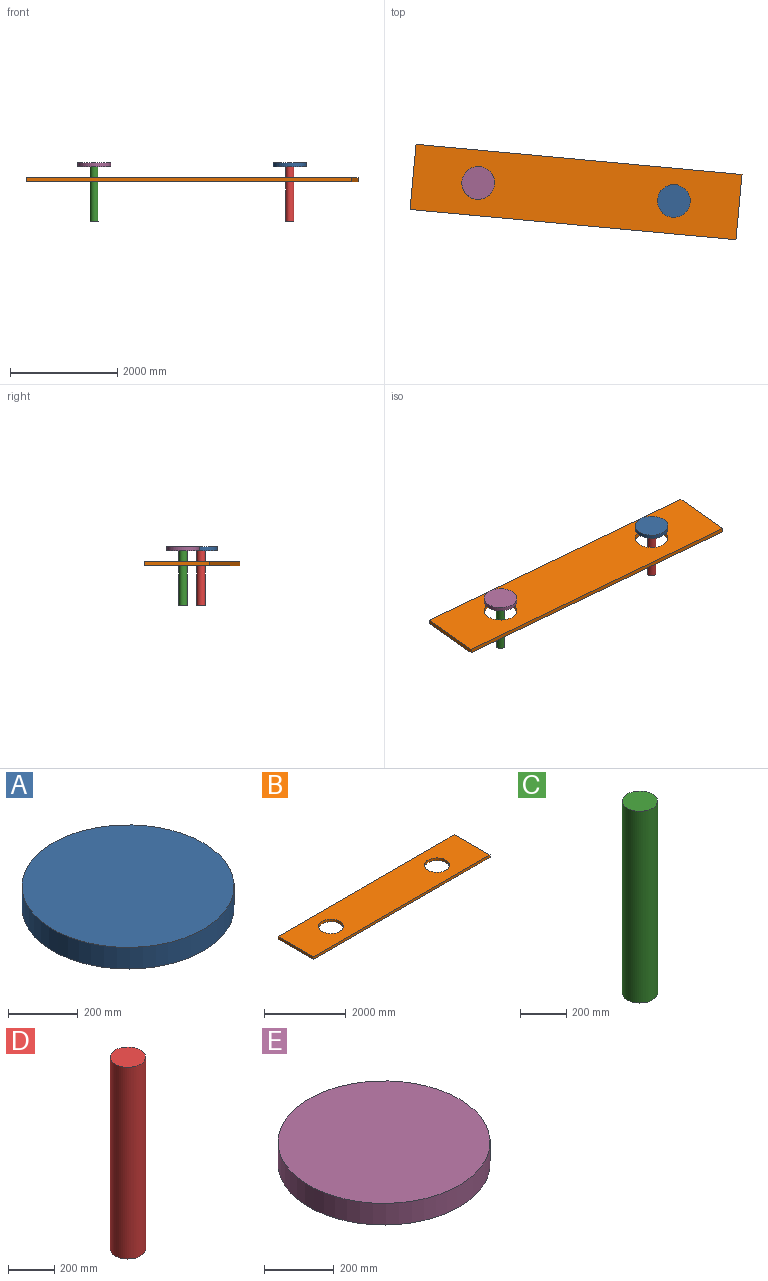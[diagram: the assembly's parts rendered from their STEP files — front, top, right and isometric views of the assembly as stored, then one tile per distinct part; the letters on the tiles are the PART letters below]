
ASSEMBLY  parts=5 mates=3
PART A: 3 faces, bbox 609.6x609.6x76.2 mm
  f0: cylinder r=304.8mm len=609.6mm, axis (0,0,-1), area 145931.8mm2, adj f1,f2
  f1: plane 609.6x609.6mm, normal (0,0,1), area 291863.5mm2, adj f0
  f2: plane 609.6x609.6mm, normal (0,0,-1), area 291863.5mm2, adj f0
PART B: 8 faces, bbox 6096x1219.2x76.2 mm
  f0: plane 1219.2x76.2mm, normal (-1,0,0), area 92903mm2, adj f1,f3,f4,f5
  f1: plane 6096x76.2mm, normal (0,-1,0), area 464515.2mm2, adj f0,f2,f4,f5
  f2: plane 1219.2x76.2mm, normal (1,0,0), area 92903mm2, adj f1,f3,f4,f5
  f3: plane 6096x76.2mm, normal (0,1,0), area 464515.2mm2, adj f0,f2,f4,f5
  f4: plane 6096x1219.2mm, normal (0,0,1), area 6848516.2mm2, adj f0,f1,f2,f3,f6,f7
  f5: plane 6096x1219.2mm, normal (0,0,-1), area 6848516.2mm2, adj f0,f1,f2,f3,f6,f7
  f6: cylinder r=304.8mm len=609.6mm, axis (0,0,1), area 145931.8mm2, adj f4,f5
  f7: cylinder r=304.8mm len=609.6mm, axis (0,0,1), area 145931.8mm2, adj f4,f5
PART C: 3 faces, bbox 152.4x152.4x1016 mm
  f0: cylinder r=76.2mm len=1016mm, axis (0,0,1), area 486439.2mm2, adj f1,f2
  f1: plane 152.4x152.4mm, normal (0,0,-1), area 18241.5mm2, adj f0
  f2: plane 152.4x152.4mm, normal (0,0,1), area 18241.5mm2, adj f0
PART D: 3 faces, bbox 152.4x152.4x1016 mm
  f0: cylinder r=76.2mm len=1016mm, axis (0,0,1), area 486439.2mm2, adj f1,f2
  f1: plane 152.4x152.4mm, normal (0,0,-1), area 18241.5mm2, adj f0
  f2: plane 152.4x152.4mm, normal (0,0,1), area 18241.5mm2, adj f0
PART E: 3 faces, bbox 609.6x609.6x76.2 mm
  f0: cylinder r=304.8mm len=609.6mm, axis (0,0,-1), area 145931.8mm2, adj f1,f2
  f1: plane 609.6x609.6mm, normal (0,0,1), area 291863.5mm2, adj f0
  f2: plane 609.6x609.6mm, normal (0,0,-1), area 291863.5mm2, adj f0
PLACE A rot(axis=(0,0,-1),161.5deg) t=(8488.36,1438.25,776.77)mm
PLACE B rot(axis=(0,0,-1),5.3deg) t=(1695.69,650.46,494.25)mm
PLACE C t=(4640.34,1145.24,776.77)mm
PLACE D rot(axis=(0,0,-1),161.5deg) t=(8488.36,1438.25,776.77)mm
PLACE E t=(4640.34,1145.24,776.77)mm
MATE planar A.f0 <-> E.f0  axis (0,0,1) through (6607.9,808.54,852.97)mm
MATE cylindrical D.f0 <-> B.f7  axis (0,0,1) through (6607.9,808.54,268.77)mm
MATE cylindrical C.f0 <-> B.f6  axis (0,0,1) through (2965.83,1145.24,268.77)mm
